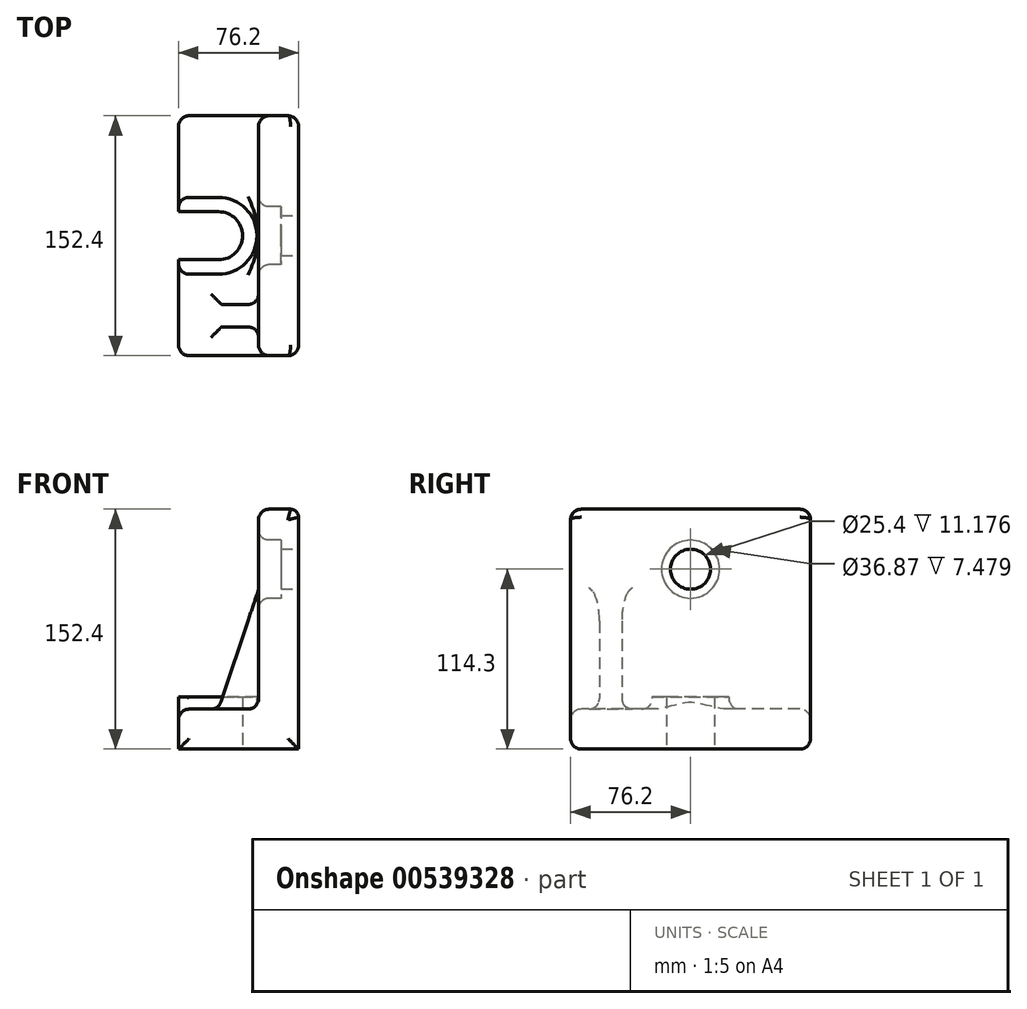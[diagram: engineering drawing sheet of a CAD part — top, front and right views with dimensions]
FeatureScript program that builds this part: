
annotation { "Feature Type Name" : "Feature", "Feature Type Description" : "" }
export const myFeature = defineFeature(function(context is Context, id is Id, definition is map)
    precondition{}
    {
        {
            var Q0;
            Q0=qCreatedBy(makeId("Front.planeOp"),FACE);
            var sketch = newSketch(context, id + "F0", { "sketchPlane" : qUnion([Q0])});
            skLineSegment(sketch, "E0", {"start": v(0, 152.4) * mm, "end": v(0, 0) * mm});
            skLineSegment(sketch, "E1", {"start": v(0, 0) * mm, "end": v(-76.2, 0) * mm});
            skLineSegment(sketch, "E2", {"start": v(-76.2, 0) * mm, "end": v(-76.2, 25.4) * mm});
            skLineSegment(sketch, "E3", {"start": v(-76.2, 25.4) * mm, "end": v(-25.4, 25.4) * mm});
            skLineSegment(sketch, "E4", {"start": v(-25.4, 25.4) * mm, "end": v(-25.4, 152.4) * mm});
            skLineSegment(sketch, "E5", {"start": v(-25.4, 152.4) * mm, "end": v(0, 152.4) * mm});
            skSolve(sketch);
        }
        {
            var Q0;
            Q0=makeQuery(id+"F0.imprint","IMPRINT",FACE,{"disambiguationData":[TD([[makeQuery(id+"F0.imprint","IMPRINT",EDGE,{"derivedFrom":sQuery(id+"F0.wireOp",EDGE,"E0")}),-1.0]])]});
            extrude(context, id + "F1", {"entities" : qUnion([Q0]), "endBound" : BoundingType.SYMMETRIC, "oppositeDirection" : true, "depth" : 152.4 * mm, "offsetDistance" : 25.4 * mm});
        }
        {
            var Q0;
            Q0=makeQuery(id+"F1.opExtrude","SWEPT_FACE",FACE,{"disambiguationData":[OSD([sQuery(id+"F0.wireOp",EDGE,"E0")])]});
            var sketch = newSketch(context, id + "F2", { "sketchPlane" : qUnion([Q0])});
            skLineSegment(sketch, "E6", {"start": v(0, 0) * mm, "end": v(0, 102.25) * mm, "construction": true});
            skSolve(sketch);
        }
        {
            var Q0;
            {var subQ0=sQuery(id+"F0.wireOp",EDGE,"E0");Q0=makeQuery(id+"F2.imprint","IMPRINT",FACE,{"disambiguationData":[TD([[makeQuery(id+"F2.imprint","IMPRINT",EDGE,{"derivedFrom":makeQuery(id+"F1.opExtrude","CAP_EDGE",EDGE,{"disambiguationData":[OSD([subQ0])],"isStart":true})}),1.0]])]});}
            var sketch = newSketch(context, id + "F3", { "sketchPlane" : qUnion([Q0])});
            skCircle(sketch, "E7", {"center": v(0, 114.3) * mm, "radius": 12.7 * mm});
            skSolve(sketch);
        }
        {
            var Q0;
            Q0=makeQuery(id+"F3.imprint","IMPRINT",FACE,{"disambiguationData":[TD([[makeQuery(id+"F3.imprint","IMPRINT",EDGE,{"derivedFrom":sQuery(id+"F3.wireOp",EDGE,"E7")}),1.0]])]});
            extrude(context, id + "F4", {"entities" : qUnion([Q0]), "operationType" : NewBodyOperationType.REMOVE, "endBound" : BoundingType.THROUGH_ALL, "oppositeDirection" : true, "depth" : 28.2 * mm, "offsetDistance" : 25.4 * mm});
        }
        {
            var Q0;
            Q0=makeQuery(id+"F1.opExtrude","SWEPT_FACE",FACE,{"disambiguationData":[OSD([sQuery(id+"F0.wireOp",EDGE,"E1")])]});
            var sketch = newSketch(context, id + "F5", { "sketchPlane" : qUnion([Q0])});
            skCircle(sketch, "E8", {"center": v(-50.8, 0) * mm, "radius": 15.24 * mm});
            skPoint(sketch, "E8.centerSnap0", {"position": v(-76.2, 0) * mm});
            skLineSegment(sketch, "E9", {"start": v(-50.8, -15.24) * mm, "end": v(-76.2, -15.24) * mm});
            skLineSegment(sketch, "E10", {"start": v(-50.8, 15.24) * mm, "end": v(-76.2, 15.24) * mm});
            skSolve(sketch);
        }
        {
            var Q0;
            {var subQ0=sQuery(id+"F5.wireOp",EDGE,"E8");var subQ1=makeQuery(id+"F5.imprint","INTERSECT",VERTEX,{"derivedFrom":[subQ0,sQuery(id+"F5.wireOp",EDGE,"E9")]});Q0=makeQuery(id+"F5.imprint","IMPRINT",FACE,{"disambiguationData":[TD([[makeQuery(id+"F5.imprint","IMPRINT",EDGE,{"disambiguationData":[TD([[subQ1,1.0]])],"derivedFrom":subQ0}),1.0]])]});}
            var Q1;
            {var subQ0=sQuery(id+"F5.wireOp",EDGE,"E9");Q1=makeQuery(id+"F5.imprint","IMPRINT",FACE,{"disambiguationData":[TD([[makeQuery(id+"F5.imprint","IMPRINT",EDGE,{"derivedFrom":subQ0}),-1.0]])]});}
            extrude(context, id + "F6", {"entities" : qUnion([Q0, Q1]), "operationType" : NewBodyOperationType.REMOVE, "endBound" : BoundingType.THROUGH_ALL, "oppositeDirection" : true, "depth" : 25.4 * mm, "offsetDistance" : 25.4 * mm});
        }
        {
            var Q0;
            Q0=qCreatedBy(makeId("Front.planeOp"),FACE);
            cPlane(context, id + "F7", {"entities" : qUnion([Q0]), "cplaneType" : CPlaneType.OFFSET, "offset" : 50.8 * mm, "width" : 152.4 * mm, "height" : 152.4 * mm});
        }
        {
            var Q0;
            Q0=qCreatedBy(id+"F7.planeOp",FACE);
            var sketch = newSketch(context, id + "F8", { "sketchPlane" : qUnion([Q0])});
            skLineSegment(sketch, "E11.0", {"start": v(-25.4, 25.4) * mm, "end": v(-25.4, 101.6) * mm});
            skLineSegment(sketch, "E12.0", {"start": v(-50.8, 25.4) * mm, "end": v(-25.4, 25.4) * mm});
            skLineSegment(sketch, "E13", {"start": v(-25.4, 101.6) * mm, "end": v(-50.8, 25.4) * mm});
            skSolve(sketch);
        }
        {
            var Q0;
            Q0=makeQuery(id+"F8.imprint","IMPRINT",FACE,{"disambiguationData":[TD([[makeQuery(id+"F8.imprint","IMPRINT",EDGE,{"derivedFrom":sQuery(id+"F8.wireOp",EDGE,"E11.0")}),1.0]])]});
            extrude(context, id + "F9", {"entities" : qUnion([Q0]), "operationType" : NewBodyOperationType.ADD, "endBound" : BoundingType.SYMMETRIC, "depth" : 14.22 * mm, "offsetDistance" : 25.4 * mm});
        }
        {
            var Q0;
            Q0=makeQuery(id+"F1.opExtrude","SWEPT_FACE",FACE,{"disambiguationData":[OSD([sQuery(id+"F0.wireOp",EDGE,"E4")])]});
            var sketch = newSketch(context, id + "F10", { "sketchPlane" : qUnion([Q0])});
            skCircle(sketch, "E14", {"center": v(0, 114.3) * mm, "radius": 18.44 * mm});
            skSolve(sketch);
        }
        {
            var Q0;
            Q0 = qSketchRegion(id + "F10", true);
            extrude(context, id + "F11", {"entities" : qUnion([Q0]), "operationType" : NewBodyOperationType.REMOVE, "oppositeDirection" : true, "depth" : 14.22 * mm, "offsetDistance" : 25.4 * mm});
        }
        {
            var Q0;
            Q0=makeQuery(id+"F1.opExtrude","SWEPT_FACE",FACE,{"disambiguationData":[OSD([sQuery(id+"F0.wireOp",EDGE,"E3")])]});
            var sketch = newSketch(context, id + "F12", { "sketchPlane" : qUnion([Q0])});
            skArc(sketch, "E15.0", {"start": v(-50.8, 15.24) * mm, "mid": v(-35.56, 0) * mm, "end": v(-50.8, -15.24) * mm});
            skLineSegment(sketch, "E15.1", {"start": v(-50.8, -15.24) * mm, "end": v(-76.2, -15.24) * mm});
            skLineSegment(sketch, "E15.2", {"start": v(-50.8, 15.24) * mm, "end": v(-76.2, 15.24) * mm});
            skLineSegment(sketch, "E16.0", {"start": v(-50.8, 24.38) * mm, "end": v(-76.2, 24.38) * mm});
            skArc(sketch, "E16.1", {"start": v(-50.8, 24.38) * mm, "mid": v(-26.42, 0) * mm, "end": v(-50.8, -24.38) * mm});
            skLineSegment(sketch, "E16.2", {"start": v(-50.8, -24.38) * mm, "end": v(-76.2, -24.38) * mm});
            skSolve(sketch);
        }
        {
            var Q0;
            Q0=makeQuery(id+"F12.imprint","IMPRINT",FACE,{"disambiguationData":[TD([[makeQuery(id+"F12.imprint","IMPRINT",EDGE,{"derivedFrom":sQuery(id+"F12.wireOp",EDGE,"E15.0")}),1.0]])]});
            extrude(context, id + "F13", {"entities" : qUnion([Q0]), "operationType" : NewBodyOperationType.ADD, "depth" : 7.87 * mm, "offsetDistance" : 25.4 * mm});
        }
        {
            var Q0;
            Q0=makeQuery(id+"F1.opExtrude","SWEPT_FACE",FACE,{"disambiguationData":[OSD([sQuery(id+"F0.wireOp",EDGE,"E4")])]});
            var Q1;
            Q1=makeQuery(id+"F1.opExtrude","SWEPT_FACE",FACE,{"disambiguationData":[OSD([sQuery(id+"F0.wireOp",EDGE,"E3")])]});
            var Q2;
            Q2=makeQuery(id+"F1.opExtrude","CAP_EDGE",EDGE,{"disambiguationData":[OSD([sQuery(id+"F0.wireOp",EDGE,"E2")])],"isStart":false});
            var Q3;
            Q3=makeQuery(id+"F1.opExtrude","CAP_FACE",FACE,{"disambiguationData":[OSD([sQuery(id+"F0.wireOp",EDGE,"E0"),sQuery(id+"F0.wireOp",EDGE,"E1"),sQuery(id+"F0.wireOp",EDGE,"E2"),sQuery(id+"F0.wireOp",EDGE,"E3"),sQuery(id+"F0.wireOp",EDGE,"E4"),sQuery(id+"F0.wireOp",EDGE,"E5")])],"isStart":false});
            var Q4;
            Q4=makeQuery(id+"F1.opExtrude","CAP_FACE",FACE,{"disambiguationData":[OSD([sQuery(id+"F0.wireOp",EDGE,"E0"),sQuery(id+"F0.wireOp",EDGE,"E1"),sQuery(id+"F0.wireOp",EDGE,"E2"),sQuery(id+"F0.wireOp",EDGE,"E3"),sQuery(id+"F0.wireOp",EDGE,"E4"),sQuery(id+"F0.wireOp",EDGE,"E5")])],"isStart":true});
            fillet(context, id + "F14", {"entities" : qUnion([Q0, Q1, Q2, Q3, Q4]), "radius" : 6.75 * mm, "tangentPropagation" : true, "allowEdgeOverflow" : false});
        }
        {
            var Q0;
            {var subQ0=sQuery(id+"F0.wireOp",EDGE,"E5");var subQ1=sQuery(id+"F0.wireOp",EDGE,"E4");Q0=makeQuery(id+"F14.opFillet","BLEND_FACE",FACE,{"disambiguationData":[OSD([subQ1,subQ0]),TDD([makeQuery(id+"F1.opExtrude","CAP_VERTEX",VERTEX,{"disambiguationData":[OSD([subQ1,subQ0])],"isStart":true})])]});}
            var Q1;
            {var subQ0=sQuery(id+"F0.wireOp",EDGE,"E5");Q1=makeQuery(id+"F14.opFillet","BLEND_FACE",FACE,{"disambiguationData":[OSD([subQ0]),TDD([makeQuery(id+"F1.opExtrude","CAP_EDGE",EDGE,{"disambiguationData":[OSD([subQ0])],"isStart":true})])]});}
            var Q2;
            {var subQ0=sQuery(id+"F0.wireOp",EDGE,"E5");Q2=makeQuery(id+"F14.opFillet","BLEND_FACE",FACE,{"disambiguationData":[OSD([subQ0]),TDD([makeQuery(id+"F1.opExtrude","CAP_EDGE",EDGE,{"disambiguationData":[OSD([subQ0])],"isStart":false})])]});}
            var Q3;
            {var subQ0=sQuery(id+"F0.wireOp",EDGE,"E5");var subQ1=sQuery(id+"F0.wireOp",EDGE,"E4");Q3=makeQuery(id+"F14.opFillet","BLEND_FACE",FACE,{"disambiguationData":[OSD([subQ1,subQ0]),TDD([makeQuery(id+"F1.opExtrude","CAP_VERTEX",VERTEX,{"disambiguationData":[OSD([subQ1,subQ0])],"isStart":false})])]});}
            var Q4;
            {var subQ0=sQuery(id+"F0.wireOp",EDGE,"E4");Q4=makeQuery(id+"F14.opFillet","BLEND_EDGE",EDGE,{"blendedFrom":[makeQuery(id+"F1.opExtrude","CAP_VERTEX",VERTEX,{"disambiguationData":[OSD([subQ0,sQuery(id+"F0.wireOp",EDGE,"E5")])],"isStart":true}),makeQuery(id+"F1.opExtrude","CAP_EDGE",EDGE,{"disambiguationData":[OSD([subQ0])],"isStart":true})],"blendedInto":[]});}
            var Q5;
            {var subQ0=sQuery(id+"F0.wireOp",EDGE,"E5");var subQ1=sQuery(id+"F0.wireOp",EDGE,"E4");Q5=makeQuery(id+"F14.opFillet","BLEND_EDGE",EDGE,{"blendedFrom":[makeQuery(id+"F1.opExtrude","CAP_VERTEX",VERTEX,{"disambiguationData":[OSD([subQ1,subQ0])],"isStart":true}),makeQuery(id+"F1.opExtrude","SWEPT_EDGE",EDGE,{"disambiguationData":[OSD([subQ1,subQ0])]})],"blendedInto":[]});}
            var Q6;
            {var subQ0=sQuery(id+"F0.wireOp",EDGE,"E4");Q6=makeQuery(id+"F14.opFillet","BLEND_EDGE",EDGE,{"blendedFrom":[makeQuery(id+"F1.opExtrude","CAP_EDGE",EDGE,{"disambiguationData":[OSD([subQ0])],"isStart":true}),makeQuery(id+"F1.opExtrude","SWEPT_FACE",FACE,{"disambiguationData":[OSD([subQ0])]})],"blendedInto":[makeQuery(id+"F1.opExtrude","SWEPT_FACE",FACE,{"disambiguationData":[OSD([subQ0])]})]});}
            var Q7;
            {var subQ0=sQuery(id+"F0.wireOp",EDGE,"E4");Q7=makeQuery(id+"F14.opFillet","BLEND_EDGE",EDGE,{"blendedFrom":[makeQuery(id+"F1.opExtrude","SWEPT_EDGE",EDGE,{"disambiguationData":[OSD([subQ0,sQuery(id+"F0.wireOp",EDGE,"E5")])]}),makeQuery(id+"F1.opExtrude","SWEPT_FACE",FACE,{"disambiguationData":[OSD([subQ0])]})],"blendedInto":[makeQuery(id+"F1.opExtrude","SWEPT_FACE",FACE,{"disambiguationData":[OSD([subQ0])]})]});}
            fillet(context, id + "F15", {"entities" : qUnion([Q0, Q1, Q2, Q3, Q4, Q5, Q6, Q7]), "radius" : 5.08 * mm, "tangentPropagation" : true, "allowEdgeOverflow" : false});
        }
    });
